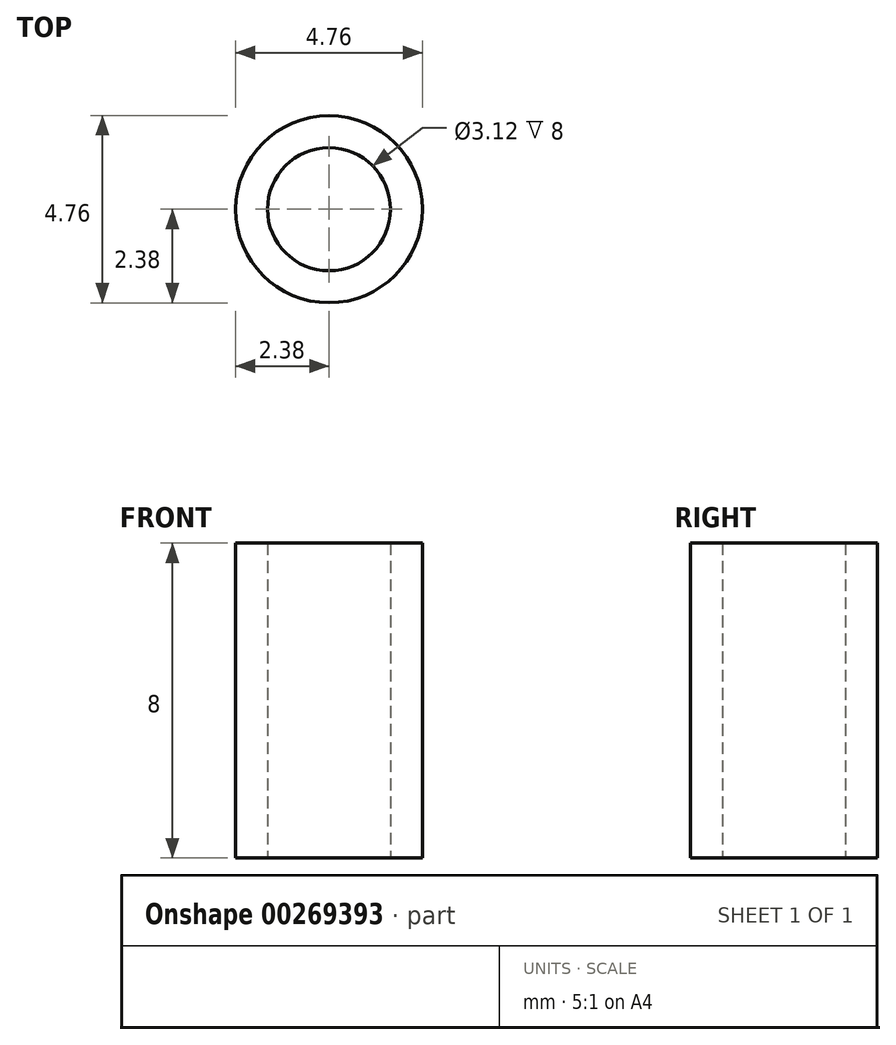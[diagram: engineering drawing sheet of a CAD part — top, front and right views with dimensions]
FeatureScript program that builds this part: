
annotation { "Feature Type Name" : "Feature", "Feature Type Description" : "" }
export const myFeature = defineFeature(function(context is Context, id is Id, definition is map)
    precondition{}
    {
        {
            var Q0;
            Q0=qCreatedBy(makeId("Top.planeOp"),FACE);
            var sketch = newSketch(context, id + "F0", { "sketchPlane" : qUnion([Q0])});
            skCircle(sketch, "E0", {"center": v(0, 0) * mm, "radius": 2.38 * mm});
            skCircle(sketch, "E1", {"center": v(0, 0) * mm, "radius": 1.56 * mm});
            skSolve(sketch);
        }
        {
            var Q0;
            Q0=makeQuery(id+"F0.imprint","IMPRINT",FACE,{"disambiguationData":[TD([[makeQuery(id+"F0.imprint","IMPRINT",EDGE,{"derivedFrom":sQuery(id+"F0.wireOp",EDGE,"E0")}),1.0]])]});
            extrude(context, id + "F1", {"entities" : qUnion([Q0]), "endBound" : BoundingType.SYMMETRIC, "depth" : 8 * mm});
        }
    });
